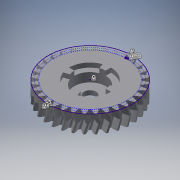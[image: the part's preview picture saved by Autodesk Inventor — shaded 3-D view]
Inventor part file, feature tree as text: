
AUTODESK INVENTOR PART (.ipt)
format: ipt  version: 2017 (Build 210142000, 142)  size: 940,544 bytes
history: native  units: mm
features: sketch x5, extrude x5, pattern_circular x3, helix x2, projected_geometry x1
ambient origin geometry x8: Origin, YZ Plane, XZ Plane, XY Plane, X Axis, Y Axis, Z Axis, Center Point
bodies: Solid1 (feature_tree)
feature tree (16):
  sketch  "Sketch1"  dims[d0=20.0mm d1=0.0mm]
  extrude  "Extrusion1"  TaperAngle=0.0deg  [1 undecoded]
  extrude  "Extrusion2"  Depth=320.0mm TaperAngle=360.0deg
  pattern_circular  "Circular Pattern1"  [2 undecoded]
  extrude  "Extrusion3"  Depth=6.0mm
  extrude  "Extrusion4"  Depth=12.217305mm
  extrude  "Extrusion5"  Depth=5.0mm TaperAngle=0.0deg
  pattern_circular  "Circular Pattern2"  Count=4 Angle=360.0deg
  helix  "Coil1"  [1 undecoded]
  helix  "Coil2"  [1 undecoded]
  pattern_circular  "Circular Pattern3"  [2 undecoded]
  sketch  "Sketch2"  dims[d2=10.0mm d3=0.0mm d4=320.0mm d5=360.0deg]
  sketch  "Sketch3"  dims[d7=13.5mm]
  sketch  "Sketch4"  dims[d8=10.0mm d9=0.0mm]
  sketch  "Sketch5"  dims[d10=35.0mm d11=15.0mm d12=0.0mm d13=6.0mm d14=12.217305mm d15=5.0mm d16=0.0mm d17=40.0mm d18=360.0deg d20=10.0mm d21=10.0mm d22=0.1mm d23=0.0mm d24=90.0deg d25=90.0deg d26=0.0mm d27=0.0mm d28=10.0mm d29=10.0mm d30=0.1mm d31=0.0mm d32=90.0deg d33=90.0deg d34=0.0mm d35=0.0mm d36=320.0mm d37=360.0deg]
  projected_geometry  "Projected Loop1"
note: 7 required parameter values undecoded (feature->parameter linkage not recoverable at this tier; creation-order binding heuristic only, values carry confidence <= 0.55)
